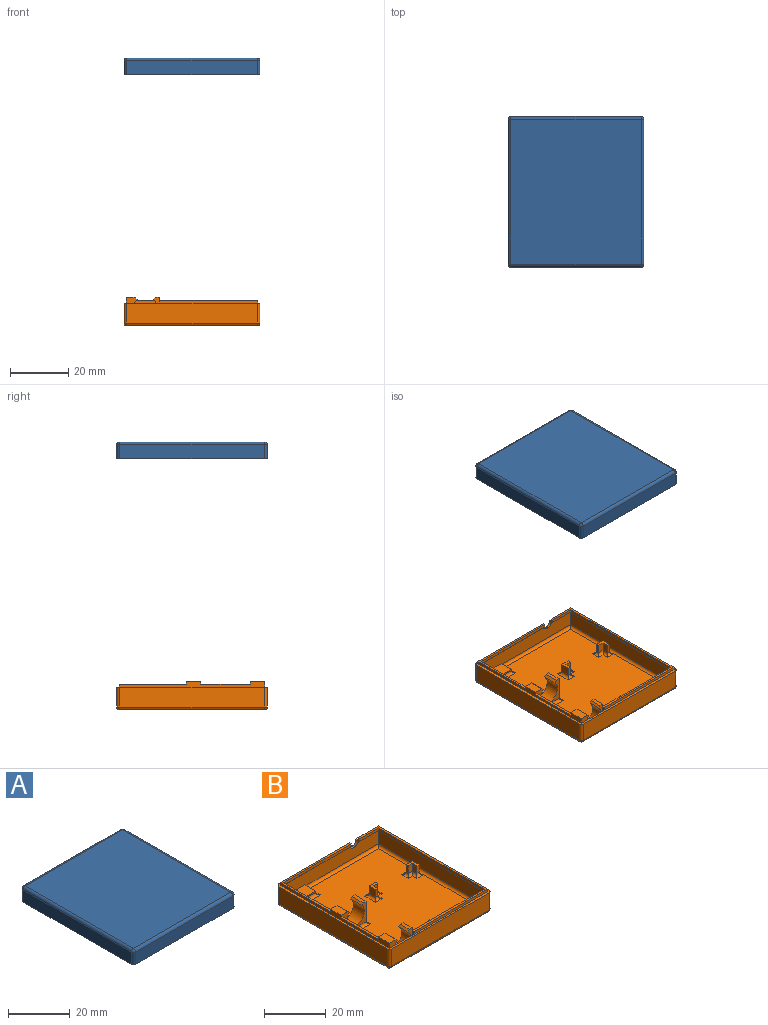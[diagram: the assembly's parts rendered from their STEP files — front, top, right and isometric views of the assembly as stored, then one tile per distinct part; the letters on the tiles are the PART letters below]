
ASSEMBLY  parts=2 mates=2
PART A: 28 faces, bbox 46.6x51.6x5.8 mm
  f0: plane 45x4mm, normal (0,-1,0), area 174.3mm2, adj f6,f7,f9,f11,f14
  f1: plane 44.6x4.8mm, normal (0,1,0), area 208.4mm2, adj f9,f11,f18,f24,f27
  f2: plane 49.6x4.8mm, normal (-1,0,0), area 238.1mm2, adj f9,f21,f25,f27
  f3: plane 44.6x4.8mm, normal (0,-1,0), area 214.1mm2, adj f9,f16,f20,f21
  f4: plane 49.6x4.8mm, normal (1,0,0), area 238.1mm2, adj f9,f16,f18,f19
  f5: plane 49.6x44.6mm, normal (0,0,1), area 2212.2mm2, adj f19,f20,f24,f25
  f6: plane 50x4mm, normal (1,0,0), area 200mm2, adj f0,f8,f9,f12
  f7: plane 50x4mm, normal (-1,0,0), area 200mm2, adj f0,f8,f9,f15
  f8: plane 45x4mm, normal (0,1,0), area 180mm2, adj f6,f7,f9,f13
  f9: plane 51.6x46.6mm, normal (0,0,-1), area 150.7mm2, adj f0,f1,f2,f3,f4,f6,f7,f8
  f10: plane 48x43mm, normal (0,0,-1), area 2064mm2, adj f12,f13,f14,f15
  f11: cylinder r=1.9mm len=3.8mm, axis (0,1,0), area 4.8mm2, adj f0,f1,f9
  f12: cylinder r=1mm len=50mm, axis (0,1,0), area 77.4mm2, adj f6,f10,f13,f14
  f13: cylinder r=1mm len=45mm, axis (-1,0,0), area 69.5mm2, adj f8,f10,f12,f15
  f14: cylinder r=1mm len=45mm, axis (1,0,0), area 69.5mm2, adj f0,f10,f12,f15
  f15: cylinder r=1mm len=50mm, axis (0,-1,0), area 77.4mm2, adj f7,f10,f13,f14
  f16: cylinder r=1mm len=4.8mm, axis (0,0,-1), area 7.5mm2, adj f3,f4,f9,f17
  f17: sphere r=1mm, area 1.6mm2, adj f16,f19,f20
  f18: cylinder r=1mm len=4.8mm, axis (0,0,1), area 7.5mm2, adj f1,f4,f9,f22
  f19: cylinder r=1mm len=49.6mm, axis (0,-1,0), area 77.9mm2, adj f4,f5,f17,f22
  f20: cylinder r=1mm len=44.6mm, axis (-1,0,0), area 70.1mm2, adj f3,f5,f17,f23
  f21: cylinder r=1mm len=4.8mm, axis (0,0,1), area 7.5mm2, adj f2,f3,f9,f23
  f22: sphere r=1mm, area 1.6mm2, adj f18,f19,f24
  f23: sphere r=1mm, area 1.6mm2, adj f20,f21,f25
  f24: cylinder r=1mm len=44.6mm, axis (1,0,0), area 70.1mm2, adj f1,f5,f22,f26
  f25: cylinder r=1mm len=49.6mm, axis (0,1,0), area 77.9mm2, adj f2,f5,f23,f26
  f26: sphere r=1mm, area 1.6mm2, adj f24,f25,f27
  f27: cylinder r=1mm len=4.8mm, axis (0,0,-1), area 7.5mm2, adj f1,f2,f9,f26
PART B: 129 faces, bbox 46.6x51.6x9.8 mm
  f0: plane 31.67x23mm, normal (0,0,1), area 43.1mm2, adj f3,f4,f15,f34,f40,f127
  f1: plane 45x5.2mm, normal (0,-1,0), area 225.6mm2, adj f5,f6,f13,f14,f35,f36,f98,f128
  f2: plane 51.6x46.6mm, normal (0,0,1), area 150.7mm2, adj f3,f8,f12,f16,f17,f18,f19,f32
  f3: plane 31.67x1mm, normal (0,1,0), area 31.7mm2, adj f0,f2,f34,f127
  f4: plane 30.87x1mm, normal (0,-1,0), area 30.9mm2, adj f0,f5,f40,f127
  f5: plane 31.87x0.82mm, normal (0,-0.71,-0.71), area 35.4mm2, adj f1,f4,f47,f128
  f6: plane 9.72x0.82mm, normal (0,-0.71,-0.71), area 10.4mm2, adj f1,f41,f49,f128
  f7: plane 8x5mm, normal (1,0,0), area 35.5mm2, adj f10,f12,f24,f99,f123,f124
  f8: plane 33.7x1mm, normal (0,-1,0), area 33.7mm2, adj f2,f38,f44,f125
  f9: plane 17x5.2mm, normal (1,0,0), area 88.4mm2, adj f10,f11,f50,f88
  f10: plane 11.3x8mm, normal (0,1,0), area 39.3mm2, adj f7,f9,f21,f22,f23,f24,f33,f34
  f11: plane 11.3x8mm, normal (0,-1,0), area 39.3mm2, adj f9,f25,f26,f27,f28,f29,f30,f34
  f12: plane 42.5x6mm, normal (0,1,0), area 214.8mm2, adj f2,f7,f13,f33,f48,f100,f124,f125
  f13: plane 50x5.2mm, normal (-1,0,0), area 260mm2, adj f1,f12,f49,f97
  f14: plane 23x5.2mm, normal (1,0,0), area 117.1mm2, adj f1,f15,f36,f37,f47,f82
  f15: plane 11.3x8mm, normal (0,1,0), area 39.3mm2, adj f0,f14,f25,f26,f27,f28,f29,f30
  f16: plane 44.6x6.8mm, normal (0,1,0), area 297.6mm2, adj f2,f116,f119,f122,f128
  f17: plane 49.6x6.8mm, normal (-1,0,0), area 337.3mm2, adj f2,f111,f116,f117
  f18: plane 44.6x6.8mm, normal (0,-1,0), area 303.3mm2, adj f2,f111,f112,f113
  f19: plane 49.6x6.8mm, normal (1,0,0), area 337.3mm2, adj f2,f113,f118,f119
  f20: plane 49.6x44.6mm, normal (0,0,-1), area 2212.2mm2, adj f112,f117,f118,f122
  f21: plane 5x3mm, normal (0,0,1), area 15mm2, adj f10,f22,f32,f34
  f22: plane 5x0.67mm, normal (0.71,0,0.71), area 4.7mm2, adj f10,f21,f32,f33
  f23: plane 4.1x0.67mm, normal (-0.71,0,0.71), area 3.9mm2, adj f10,f24,f33,f123
  f24: plane 4.1x1.3mm, normal (0,0,1), area 5.3mm2, adj f7,f10,f23,f123
  f25: plane 8x5mm, normal (1,0,0), area 40mm2, adj f11,f15,f26,f80
  f26: plane 5x1.3mm, normal (0,0,1), area 6.5mm2, adj f11,f15,f25,f27
  f27: plane 5x0.67mm, normal (-0.71,0,0.71), area 4.7mm2, adj f11,f15,f26,f28
  f28: cylinder r=4mm len=8mm, axis (0,-1,0), area 94.2mm2, adj f11,f15,f27,f29
  f29: plane 5x0.67mm, normal (0.71,0,0.71), area 4.7mm2, adj f11,f15,f28,f30
  f30: plane 5x3mm, normal (0,0,1), area 15mm2, adj f11,f15,f29,f34
  f31: plane 48x43mm, normal (0,0,1), area 1787.9mm2, adj f79,f80,f81,f82,f83,f84,f85,f86
  f32: plane 3.67x2mm, normal (0,-1,0), area 6.4mm2, adj f2,f21,f22,f33,f34
  f33: cylinder r=4mm len=8mm, axis (0,-1,0), area 90mm2, adj f10,f12,f22,f23,f32,f123,f124
  f34: plane 50x2mm, normal (-1,0,0), area 60mm2, adj f0,f2,f3,f10,f11,f15,f21,f30
  f35: plane 5x0.5mm, normal (1,0,0), area 2.5mm2, adj f1,f36,f37,f93
  f36: plane 11.3x5mm, normal (0,0,1), area 56.5mm2, adj f1,f14,f35,f37
  f37: plane 11.3x0.5mm, normal (0,-1,0), area 5.7mm2, adj f14,f35,f36,f87
  f38: plane 50x1mm, normal (1,0,0), area 50mm2, adj f2,f8,f39,f44
  f39: plane 9.53x1mm, normal (0,1,0), area 9.5mm2, adj f2,f38,f44,f126
  f40: plane 22.2x1mm, normal (1,0,0), area 22.2mm2, adj f0,f4,f15,f47
  f41: plane 8.73x1mm, normal (0,-1,0), area 8.7mm2, adj f6,f42,f44,f126
  f42: plane 48.4x1mm, normal (-1,0,0), area 48.4mm2, adj f41,f43,f44,f49
  f43: plane 32.9x1mm, normal (0,1,0), area 32.9mm2, adj f42,f44,f48,f125
  f44: plane 50x33.7mm, normal (0,0,1), area 73.3mm2, adj f8,f38,f39,f41,f42,f43,f125,f126
  f45: plane 17x1mm, normal (1,0,0), area 17mm2, adj f10,f11,f46,f50
  f46: plane 17x0.8mm, normal (0,0,1), area 13.6mm2, adj f10,f11,f34,f45
  f47: plane 23x0.8mm, normal (0.71,0,-0.71), area 25.6mm2, adj f5,f14,f15,f40
  f48: plane 33.7x0.8mm, normal (0,0.71,-0.71), area 37.7mm2, adj f12,f43,f49,f125
  f49: plane 50x0.8mm, normal (-0.71,0,-0.71), area 55.7mm2, adj f6,f13,f42,f48
  f50: plane 17x0.8mm, normal (0.71,0,-0.71), area 19.2mm2, adj f9,f10,f11,f45
  f51: plane 3x3mm, normal (0,1,0), area 9mm2, adj f52,f56,f57,f105
  f52: plane 3x3mm, normal (-1,0,0), area 9mm2, adj f51,f53,f57,f107
  f53: plane 3x1mm, normal (0,-1,0), area 3mm2, adj f52,f54,f57,f109
  f54: plane 3x2mm, normal (1,0,0), area 6mm2, adj f53,f55,f57,f110
  f55: plane 3x2mm, normal (0,-1,0), area 6mm2, adj f54,f56,f57,f108
  f56: plane 3x1mm, normal (1,0,0), area 3mm2, adj f51,f55,f57,f106
  f57: plane 3x3mm, normal (0,0,1), area 5mm2, adj f51,f52,f53,f54,f55,f56
  f58: plane 3x1mm, normal (0,-1,0), area 3mm2, adj f59,f63,f64,f91
  f59: plane 3x3mm, normal (1,0,0), area 9mm2, adj f58,f60,f64,f97
  f60: plane 3x3mm, normal (0,1,0), area 9mm2, adj f59,f61,f64,f92
  f61: plane 3x1mm, normal (-1,0,0), area 3mm2, adj f60,f62,f64,f86
  f62: plane 3x2mm, normal (0,-1,0), area 6mm2, adj f61,f63,f64,f81
  f63: plane 3x2mm, normal (-1,0,0), area 6mm2, adj f58,f62,f64,f85
  f64: plane 3x3mm, normal (0,0,1), area 5mm2, adj f58,f59,f60,f61,f62,f63
  f65: plane 3x1mm, normal (0,1,0), area 3mm2, adj f66,f70,f71,f89
  f66: plane 3x3mm, normal (-1,0,0), area 9mm2, adj f65,f67,f71,f95
  f67: plane 3x3mm, normal (0,-1,0), area 9mm2, adj f66,f68,f71,f100
  f68: plane 3x1mm, normal (1,0,0), area 3mm2, adj f67,f69,f71,f96
  f69: plane 3x2mm, normal (0,1,0), area 6mm2, adj f68,f70,f71,f90
  f70: plane 3x2mm, normal (1,0,0), area 6mm2, adj f65,f69,f71,f84
  f71: plane 3x3mm, normal (0,0,1), area 5mm2, adj f65,f66,f67,f68,f69,f70
  f72: plane 3x3mm, normal (1,0,0), area 9mm2, adj f73,f77,f78,f97
  f73: plane 3x1mm, normal (0,1,0), area 3mm2, adj f72,f74,f78,f101
  f74: plane 3x2mm, normal (-1,0,0), area 6mm2, adj f73,f75,f78,f103
  f75: plane 3x2mm, normal (0,1,0), area 6mm2, adj f74,f76,f78,f104
  f76: plane 3x1mm, normal (-1,0,0), area 3mm2, adj f75,f77,f78,f102
  f77: plane 3x3mm, normal (0,-1,0), area 9mm2, adj f72,f76,f78,f100
  f78: plane 3x3mm, normal (0,0,1), area 5mm2, adj f72,f73,f74,f75,f76,f77
  f79: cylinder r=1mm len=12.3mm, axis (-1,0,0), area 17.7mm2, adj f15,f31,f80,f82
  f80: cylinder r=1mm len=7mm, axis (0,1,0), area 9mm2, adj f25,f31,f79,f83
  f81: cylinder r=1mm len=3mm, axis (1,0,0), area 3.1mm2, adj f31,f62,f85,f86
  f82: cylinder r=1mm len=18mm, axis (0,1,0), area 27.1mm2, adj f14,f31,f79,f87
  f83: cylinder r=1mm len=12.3mm, axis (1,0,0), area 17.7mm2, adj f11,f31,f80,f88
  f84: cylinder r=1mm len=3mm, axis (0,1,0), area 3.1mm2, adj f31,f70,f89,f90
  f85: cylinder r=1mm len=3mm, axis (0,-1,0), area 3.1mm2, adj f31,f63,f81,f91
  f86: cylinder r=1mm len=3mm, axis (0,-1,0), area 2.7mm2, adj f31,f61,f81,f92
  f87: cylinder r=1mm len=12.3mm, axis (1,0,0), area 17.7mm2, adj f31,f37,f82,f93
  f88: cylinder r=1mm len=17mm, axis (0,1,0), area 25.6mm2, adj f9,f31,f83,f94
  f89: cylinder r=1mm len=3mm, axis (-1,0,0), area 2.7mm2, adj f31,f65,f84,f95
  f90: cylinder r=1mm len=3mm, axis (-1,0,0), area 3.1mm2, adj f31,f69,f84,f96
  f91: cylinder r=1mm len=3mm, axis (1,0,0), area 2.7mm2, adj f31,f58,f85,f97
  f92: cylinder r=1mm len=5mm, axis (-1,0,0), area 5.9mm2, adj f31,f60,f86,f97
  f93: cylinder r=1mm len=6mm, axis (0,1,0), area 7.9mm2, adj f31,f35,f87,f98
  f94: cylinder r=1mm len=12.3mm, axis (-1,0,0), area 17.7mm2, adj f10,f31,f88,f99
  f95: cylinder r=1mm len=5mm, axis (0,-1,0), area 5.9mm2, adj f31,f66,f89,f100
  f96: cylinder r=1mm len=3mm, axis (0,1,0), area 2.7mm2, adj f31,f68,f90,f100
  f97: cylinder r=1mm len=50mm, axis (0,1,0), area 89.1mm2, adj f13,f31,f59,f72,f91,f92,f98,f100
  f98: cylinder r=1mm len=33.7mm, axis (1,0,0), area 51.8mm2, adj f1,f31,f93,f97
  f99: cylinder r=1mm len=6mm, axis (0,1,0), area 7.9mm2, adj f7,f31,f94,f100
  f100: cylinder r=1mm len=33.7mm, axis (1,0,0), area 63.5mm2, adj f12,f31,f67,f77,f95,f96,f97,f99
  f101: cylinder r=1mm len=3mm, axis (-1,0,0), area 2.7mm2, adj f31,f73,f97,f103
  f102: cylinder r=1mm len=3mm, axis (0,-1,0), area 2.7mm2, adj f31,f76,f100,f104
  f103: cylinder r=1mm len=3mm, axis (0,-1,0), area 3.1mm2, adj f31,f74,f101,f104
  f104: cylinder r=1mm len=3mm, axis (-1,0,0), area 3.1mm2, adj f31,f75,f102,f103
  f105: cylinder r=1mm len=5mm, axis (-1,0,0), area 5.9mm2, adj f31,f51,f106,f107
  f106: cylinder r=1mm len=3mm, axis (0,1,0), area 2.7mm2, adj f31,f56,f105,f108
  f107: cylinder r=1mm len=5mm, axis (0,-1,0), area 5.9mm2, adj f31,f52,f105,f109
  f108: cylinder r=1mm len=3mm, axis (1,0,0), area 3.1mm2, adj f31,f55,f106,f110
  f109: cylinder r=1mm len=3mm, axis (1,0,0), area 2.7mm2, adj f31,f53,f107,f110
  f110: cylinder r=1mm len=3mm, axis (0,1,0), area 3.1mm2, adj f31,f54,f108,f109
  f111: cylinder r=1mm len=6.8mm, axis (0,0,1), area 10.7mm2, adj f2,f17,f18,f114
  f112: cylinder r=1mm len=44.6mm, axis (1,0,0), area 70.1mm2, adj f18,f20,f114,f115
  f113: cylinder r=1mm len=6.8mm, axis (0,0,-1), area 10.7mm2, adj f2,f18,f19,f115
  f114: sphere r=1mm, area 1.6mm2, adj f111,f112,f117
  f115: sphere r=1mm, area 1.6mm2, adj f112,f113,f118
  f116: cylinder r=1mm len=6.8mm, axis (0,0,-1), area 10.7mm2, adj f2,f16,f17,f120
  f117: cylinder r=1mm len=49.6mm, axis (0,-1,0), area 77.9mm2, adj f17,f20,f114,f120
  f118: cylinder r=1mm len=49.6mm, axis (0,1,0), area 77.9mm2, adj f19,f20,f115,f121
  f119: cylinder r=1mm len=6.8mm, axis (0,0,1), area 10.7mm2, adj f2,f16,f19,f121
  f120: sphere r=1mm, area 1.6mm2, adj f116,f117,f122
  f121: sphere r=1mm, area 1.6mm2, adj f118,f119,f122
  f122: cylinder r=1mm len=44.6mm, axis (-1,0,0), area 70.1mm2, adj f16,f20,f120,f121
  f123: plane 5x1.97mm, normal (0,-1,0), area 5.7mm2, adj f7,f23,f24,f33,f124
  f124: plane 1.09x0.9mm, normal (0,0,1), area 1mm2, adj f7,f12,f33,f123
  f125: plane 1.8x0.8mm, normal (-1,0,0), area 1.1mm2, adj f8,f12,f43,f44,f48
  f126: plane 1x0.8mm, normal (-1,0,0), area 0.8mm2, adj f39,f41,f44,f128
  f127: plane 1x0.8mm, normal (1,0,0), area 0.8mm2, adj f0,f3,f4,f128
  f128: cylinder r=1.9mm len=3.8mm, axis (0,1,0), area 5.4mm2, adj f1,f2,f5,f6,f16,f126,f127
PLACE A t=(-7.15,27.39,139.26)mm
PLACE B t=(-16.43,27.39,49.05)mm
MATE planar B.f38 <-> A.f7  axis (1,0,0) through (37.85,52.39,56.55)mm
MATE planar B.f8 <-> A.f8  axis (0,-1,0) through (21,27.39,56.55)mm
